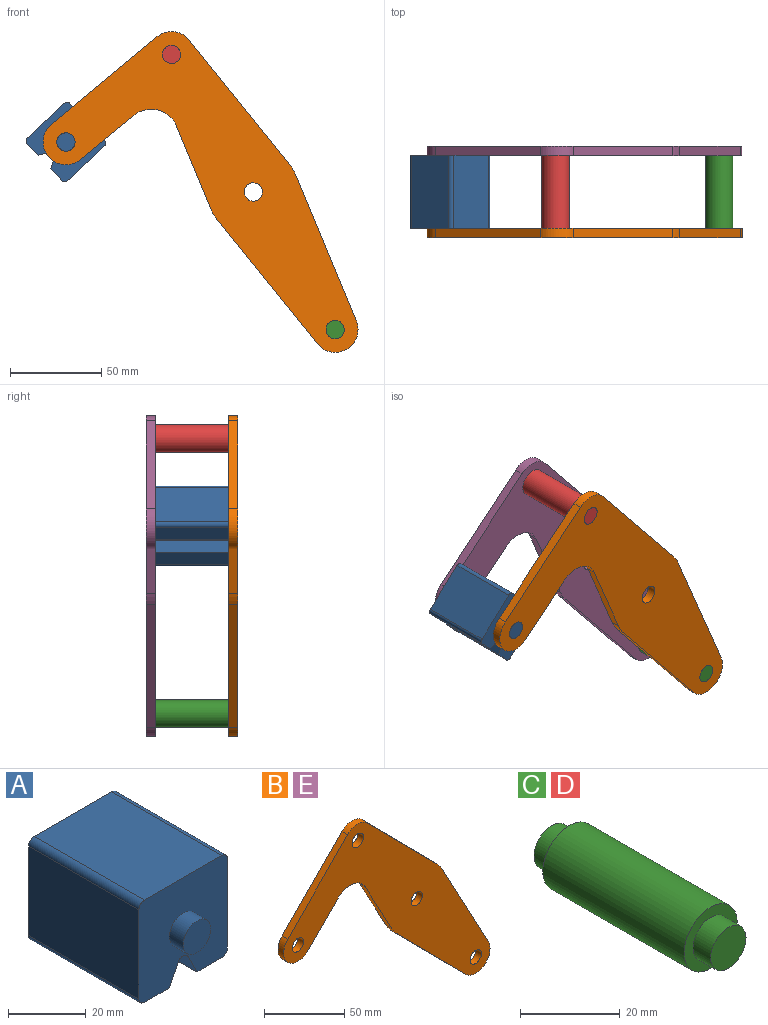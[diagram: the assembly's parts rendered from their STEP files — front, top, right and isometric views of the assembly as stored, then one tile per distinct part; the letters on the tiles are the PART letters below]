
ASSEMBLY  parts=5 mates=3
PART A: 18 faces, bbox 32.1x50x32.1 mm
  f0: plane 40x28.08mm, normal (1,0,0), area 1123.1mm2, adj f4,f10,f13,f14
  f1: plane 40x9.04mm, normal (0,0,-1), area 361.6mm2, adj f2,f4,f10,f14
  f2: plane 40x6.42mm, normal (-0.89,0,-0.45), area 287.2mm2, adj f1,f4,f10,f15
  f3: plane 40x6.42mm, normal (0.89,0,-0.45), area 287.2mm2, adj f4,f5,f10,f15
  f4: plane 32.08x32.08mm, normal (0,-1,0), area 900.6mm2, adj f0,f1,f2,f3,f5,f6,f7,f9
  f5: plane 40x9.04mm, normal (0,0,-1), area 361.6mm2, adj f3,f4,f10,f16
  f6: plane 40x28.08mm, normal (0,0,1), area 1123.1mm2, adj f4,f10,f13,f17
  f7: plane 40x28.08mm, normal (-1,0,0), area 1123.1mm2, adj f4,f10,f16,f17
  f8: plane 10x10mm, normal (0,-1,0), area 78.5mm2, adj f9
  f9: cylinder r=5mm len=10mm, axis (0,1,0), area 157.1mm2, adj f4,f8
  f10: plane 32.08x32.08mm, normal (0,1,0), area 900.6mm2, adj f0,f1,f2,f3,f5,f6,f7,f12
  f11: plane 10x10mm, normal (0,1,0), area 78.5mm2, adj f12
  f12: cylinder r=5mm len=10mm, axis (0,-1,0), area 157.1mm2, adj f10,f11
  f13: cylinder r=2mm len=40mm, axis (0,1,0), area 125.7mm2, adj f0,f4,f6,f10
  f14: cylinder r=2mm len=40mm, axis (0,-1,0), area 125.7mm2, adj f0,f1,f4,f10
  f15: cylinder r=2mm len=40mm, axis (0,1,0), area 177.1mm2, adj f2,f3,f4,f10
  f16: cylinder r=2mm len=40mm, axis (0,1,0), area 125.7mm2, adj f4,f5,f7,f10
  f17: cylinder r=2mm len=40mm, axis (0,-1,0), area 125.7mm2, adj f4,f6,f7,f10
PART B: 18 faces, bbox 181.7x5x165.8 mm
  f0: plane 43.49x23.35mm, normal (-0.88,0,-0.47), area 246.8mm2, adj f1,f14,f16,f17
  f1: cylinder r=25mm len=5.75mm, axis (0,1,0), area 35.8mm2, adj f0,f2,f16,f17
  f2: plane 61.6x60.87mm, normal (-0.71,0,-0.7), area 433mm2, adj f1,f3,f16,f17
  f3: cylinder r=12.5mm len=21.39mm, axis (0,1,0), area 178.4mm2, adj f2,f4,f16,f17
  f4: plane 76.3x40.96mm, normal (0.88,0,0.47), area 433mm2, adj f3,f5,f16,f17
  f5: cylinder r=25mm len=5.75mm, axis (0,1,0), area 35.8mm2, adj f4,f6,f16,f17
  f6: plane 61.6x60.87mm, normal (0.71,0,0.7), area 433mm2, adj f5,f7,f16,f17
  f7: cylinder r=12.5mm len=17.78mm, axis (0,1,0), area 98.9mm2, adj f6,f8,f16,f17
  f8: plane 53.35x52.71mm, normal (-0.71,0,0.7), area 375mm2, adj f7,f9,f16,f17
  f9: cylinder r=12.5mm len=21.39mm, axis (0,1,0), area 196.3mm2, adj f8,f10,f16,f17
  f10: plane 26.86x26.54mm, normal (0.71,0,-0.7), area 188.8mm2, adj f9,f14,f16,f17
  f11: cylinder r=5mm len=10mm, axis (0,1,0), area 157.1mm2, adj f16,f17
  f12: cylinder r=5mm len=10mm, axis (0,1,0), area 157.1mm2, adj f16,f17
  f13: cylinder r=5mm len=10mm, axis (0,1,0), area 157.1mm2, adj f16,f17
  f14: cylinder r=15mm len=23.89mm, axis (0,1,0), area 140.2mm2, adj f0,f10,f16,f17
  f15: cylinder r=5mm len=10mm, axis (0,1,0), area 157.1mm2, adj f16,f17
  f16: plane 181.66x165.78mm, normal (0,-1,0), area 8710.1mm2, adj f0,f1,f2,f3,f4,f5,f6,f7
  f17: plane 181.66x165.78mm, normal (0,1,0), area 8710.1mm2, adj f0,f1,f2,f3,f4,f5,f6,f7
PART C: 7 faces, bbox 15x50x15 mm
  f0: cylinder r=7.5mm len=40mm, axis (0,-1,0), area 1885mm2, adj f2,f5
  f1: cylinder r=5mm len=10mm, axis (0,1,0), area 157.1mm2, adj f2,f3
  f2: plane 15x15mm, normal (0,-1,0), area 98.2mm2, adj f0,f1
  f3: plane 10x10mm, normal (0,-1,0), area 78.5mm2, adj f1
  f4: cylinder r=5mm len=10mm, axis (0,-1,0), area 157.1mm2, adj f5,f6
  f5: plane 15x15mm, normal (0,1,0), area 98.2mm2, adj f0,f4
  f6: plane 10x10mm, normal (0,1,0), area 78.5mm2, adj f4
PART D: same geometry as C
PART E: same geometry as B
PLACE A rot(axis=(0,1,0),47.1deg) t=(0.13,-20,-0.07)mm
PLACE B rot(axis=(0,1,0),5.7deg) t=(43.82,-20,60.86)mm fixed
PLACE C rot(axis=(0,1,0),5.7deg) t=(133.28,-20,-89.55)mm
PLACE D rot(axis=(0,1,0),5.7deg) t=(43.82,-20,60.86)mm
PLACE E rot(axis=(0,1,0),5.7deg) t=(43.82,25,60.86)mm
MATE fastened C.f0 <-> B.f3  axis (0,-1,0) through (88.55,-20,-14.34)mm
MATE fastened D.f0 <-> E.f7  axis (0,1,0) through (-0.9,20,136.07)mm
MATE revolute A.f9 <-> B.f9  axis (0,-1,0) through (-58.65,-20,88.22)mm
